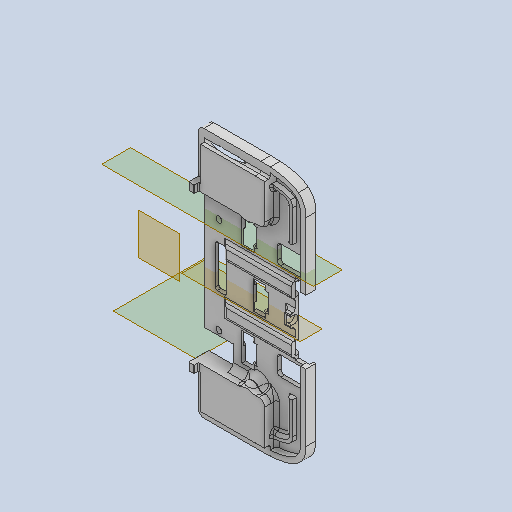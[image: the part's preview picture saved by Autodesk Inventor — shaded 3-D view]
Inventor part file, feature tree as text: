
AUTODESK INVENTOR PART (.ipt)
format: ipt  version: 2022 (Build 260153000, 153)  size: 2,006,528 bytes
history: native  units: mm
features: reference x45, extrude x29, sketch x29, other x23, projected_geometry x21, fillet x16, mirror x3, chamfer x1
ambient origin geometry x8: Origin, YZ Plane, XZ Plane, XY Plane, X Axis, Y Axis, Z Axis, Center Point
bodies: Body1 (feature_tree)
feature tree (167):
  other  "Твердое тело1"
  extrude  "Выдавливание1"  Depth=0.8mm
  other  "РабПлоскость1"
  extrude  "Выдавливание4"  Depth=0.8mm
  fillet  "Сопряжение5"  Radius=2.0mm
  other  "РабПлоскость4"
  other  "РабПлоскость5"
  other  "РабПлоскость3"
  extrude  "Выдавливание10"  Depth=0.2mm
  extrude  "Выдавливание11"  Depth=3.0mm
  extrude  "Выдавливание14"  Depth=0.8mm
  extrude  "Выдавливание16"  Depth=0.2mm
  fillet  "Сопряжение16"  Radius=3.0mm
  extrude  "Выдавливание17"  Depth=20.071286mm
  extrude  "Выдавливание22"  Depth=3.9mm TaperAngle=0.0deg
  extrude  "Выдавливание23"  Depth=0.4mm
  sketch  "Эскиз27"
  other  "РабПлоскость6"
  extrude  "Выдавливание25"  Depth=1.0mm
  extrude  "Выдавливание27"  Depth=3.490659mm
  fillet  "Сопряжение25"  Radius=0.3mm
  extrude  "Выдавливание28"  Depth=0.3mm
  fillet  "Сопряжение26"  Radius=3.9mm
  other  "РабПлоскость7"
  mirror  "Зеркальное отражение3"
  fillet  "Сопряжение29"  Radius=15.0mm
  fillet  "Сопряжение31"  Radius=10.0mm
  fillet  "Сопряжение33"  Radius=2.0mm
  extrude  "Выдавливание37"  Depth=1.5mm
  extrude  "Выдавливание38"  Depth=3.0mm
  fillet  "Сопряжение42"  Radius=7.0mm
  extrude  "Выдавливание39"  Depth=5.0mm
  extrude  "Выдавливание40"  Depth=3.0mm
  extrude  "Выдавливание41"  Depth=5.0mm
  fillet  "Сопряжение43"  Radius=3.0mm
  other  "РабПлоскость8"
  extrude  "Выдавливание42"  Depth=6.3mm TaperAngle=0.0deg
  extrude  "Выдавливание43"  Depth=2.8mm
  extrude  "Выдавливание44"  Depth=2.8mm
  fillet  "Сопряжение44"  Radius=2.8mm
  mirror  "Зеркальное отражение4"
  fillet  "Сопряжение45"  Radius=2.8mm
  extrude  "Выдавливание45"  Depth=2.8mm
  mirror  "Зеркальное отражение5"
  extrude  "Выдавливание47"  Depth=1.0mm
  extrude  "Выдавливание48"  Depth=6.3mm TaperAngle=0.0deg
  fillet  "Сопряжение47"  Radius=1.0mm
  extrude  "Выдавливание49"  Depth=3.2mm
  extrude  "Выдавливание50"  Depth=3.2mm
  fillet  "Сопряжение48"  Radius=6.3mm
  chamfer  "Фаска4"  Distance=3.0mm
  extrude  "Выдавливание51"  Depth=2.0mm TaperAngle=0.0deg
  fillet  "Сопряжение49"  Radius=0.05mm
  fillet  "Сопряжение50"  Radius=3.0mm
  extrude  "Выдавливание52"  Depth=3.0mm
  extrude  "Выдавливание53"  Depth=3.0mm
  fillet  "Сопряжение51"  Radius=3.0mm
  extrude  "Выдавливание54"  Depth=2.5mm TaperAngle=0.0deg
  sketch  "Эскиз1"
  reference  "Ссылка1"
  reference  "Ссылка2"
  reference  "Ссылка3"
  reference  "Ссылка4"
  sketch  "Эскиз4"
  projected_geometry  "Спроецированная петля3"
  reference  "Ссылка9"
  reference  "Ссылка10"
  reference  "Ссылка11"
  reference  "Ссылка12"
  reference  "Ссылка15"
  reference  "Ссылка16"
  sketch  "Эскиз11"
  projected_geometry  "Спроецированная петля9"
  sketch  "Эскиз12"
  projected_geometry  "Спроецированная петля10"
  sketch  "Эскиз15"
  projected_geometry  "Спроецированная петля13"
  reference  "Ссылка18"
  reference  "Ссылка19"
  sketch  "Эскиз18"
  reference  "Ссылка21"
  sketch  "Эскиз19"
  reference  "Ссылка22"
  sketch  "Эскиз24"
  projected_geometry  "Спроецированная петля18"
  projected_geometry  "Спроецированная петля19"
  sketch  "Эскиз25"
  reference  "Ссылка23"
  reference  "Ссылка24"
  projected_geometry  "Спроецированная петля20"
  projected_geometry  "Спроецированная петля22"
  sketch  "Эскиз29"
  reference  "Ссылка28"
  reference  "Ссылка29"
  projected_geometry  "Спроецированная петля24"
  sketch  "Эскиз30"
  reference  "Ссылка30"
  reference  "Ссылка31"
  sketch  "Эскиз40"
  projected_geometry  "Спроецированная петля34"
  sketch  "Эскиз41"
  sketch  "Эскиз42"
  reference  "Ссылка56"
  reference  "Ссылка57"
  reference  "Ссылка58"
  reference  "Ссылка59"
  reference  "Ссылка60"
  reference  "Ссылка61"
  reference  "Ссылка62"
  sketch  "Эскиз43"
  reference  "Ссылка63"
  reference  "Ссылка64"
  reference  "Ссылка65"
  reference  "Ссылка66"
  projected_geometry  "Спроецированная петля35"
  reference  "Ссылка67"
  sketch  "Эскиз44"
  projected_geometry  "Спроецированная петля36"
  sketch  "Эскиз45"
  reference  "Ссылка68"
  reference  "Ссылка69"
  reference  "Ссылка70"
  reference  "Ссылка71"
  reference  "Ссылка72"
  reference  "Ссылка73"
  reference  "Ссылка74"
  reference  "Ссылка75"
  sketch  "Эскиз46"
  reference  "Ссылка76"
  reference  "Ссылка77"
  reference  "Ссылка78"
  projected_geometry  "Спроецированная петля37"
  sketch  "Эскиз47"
  projected_geometry  "Спроецированная петля38"
  sketch  "Эскиз48"
  projected_geometry  "Спроецированная петля39"
  projected_geometry  "Спроецированная петля40"
  sketch  "Эскиз50"
  projected_geometry  "Спроецированная петля41"
  sketch  "Эскиз51"
  projected_geometry  "Спроецированная петля42"
  sketch  "Эскиз52"
  projected_geometry  "Спроецированная петля43"
  sketch  "Эскиз53"
  projected_geometry  "Спроецированная петля44"
  sketch  "Эскиз54"
  reference  "Ссылка85"
  sketch  "Эскиз55"
  projected_geometry  "Спроецированная петля45"
  sketch  "Эскиз56"
  sketch  "Эскиз57"
  reference  "Ссылка86"
  other  "<userpath>\Documents\Git\MZCAT_2024_construction\MZCAT_2024_RPI_2\MZCAT_4.iam"
  other  "MZCAT_4.iam"
  other  "commutationCATboard:1"
  other  "CAT_protector:1"
  other  "push-fit:1"
  other  "push-fit:2"
  other  "<userpath>\Documents\Git\MZCAT_2024\MZCAT_4.iam"
  other  "motherboard_key:1"
  other  "motherboard_key:2"
  other  "SMT10x2pin:1"
  other  "CAT_wheel:2"
  other  "diffuser:1"
  other  "bottom_motherboard_skeleton:1"
  other  "FastBattery:1"
  other  "metal_cap:1"
